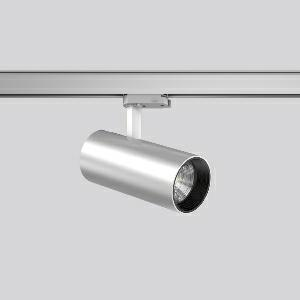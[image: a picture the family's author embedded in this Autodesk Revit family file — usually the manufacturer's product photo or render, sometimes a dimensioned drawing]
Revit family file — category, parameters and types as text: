
# Revit family: deecos_s_mini_742198_004_1_76_52b8
name_source: partatom
category: Lighting Fixtures
units: mm (PartAtom-declared; Revit-internal decimal feet)

## family parameters
Cut with Voids When Loaded = No
Host = Face
Light Source = No
Part Type = Normal
Room Calculation Point = No
Round Connector Dimension = Use Diameter
Shared = No

## types (1)
- DEECOS S mini (1 x LED Modul 940, 2400 lm, 4000)
    Apparent Load = 20 VA
    Approval mark = CE
    CIE Flux Codes = 99 100 100 100 100
    Color Rendering = 92
    Color Temperature = 4000
    Default Elevation = 1800 mm
    Description = Series: DEECOS S mini
LED surface-mounted projector in modern design with no visible cooling ribs. Housing: die-cast aluminium, powder-coated. Rotation range: 356°. Swivel range: 90°. Black plastic ring and recessed LED to prevent glare from the side. Optical assembly with lens made of plastic (polycarbonate) for the best homogeneous light distribution - can be changed without tools. Best colour rendering index Ra>90. With adapter for RZB 3-circuit DALI tracks. Suitable for Track on ceiling, Wall track. High quality converter without flickering and stroboscopic effect. The following accessories can be mounted without use of tools: interchangeable lenses, decorative glasses, honeycomb louvre, clear and frosted diffusers, white interchangeable plastic ring. 
Colour: silver
Diameter: 87 mm
Height: 214 mm
Lamp: LED
Socket: without socket
Colour temperature: 4000K
Colour rendering index (CRI): 92
System power: 20 W
Rated luminous flux: 2400 lm
Luminous efficiency: 120 lm/W
Control gear: Converter, dimmable, DALI
Protection class: I
Type of protection: IP 20
    Height = 214 mm
    Lamp = 1 x LED Modul 940
    Lamp Light Flux = 2400 lm
    Lamp count = 1
    Length = 87 mm
    Lifetime = 50000 h
    Luminous efficacy = 120 lm/W
    Manufacturer = RZB
    ModVariant = No
    Model = 742198.004.1.76
    Mounting Place = Ceiling
    Mounting Type = Rail mounted
    Number of Poles = 1
    OnlyDefault = Yes
    Power Factor = 1
    Product Name = DEECOS S mini
    Product group = Track mounted projectors
    ProductGroupID = 301
    Protection Class = Protection class I
    Protection Degree = IP 20
    RLX_Detail_Level = 1
    RLX_Emergency_Light_Flux = 0 lm
    RLX_Emergency_Type = 0
    RLX_Emergency_Type_DB = No
    RlxData = <blob elided: 37425 chars, md5=33777e1b>
    Socket = socket
    Standby Power = 0 W
    System Light Flux = 2400 lm
    System Power = 20 W
    Type Comments = Product without accessories
    Type Image = 741930.004.jpg
    URL = http://relux.com
    VarID = ---
    Voltage = 230 V
    Voltage Range = 220-240 V
    Weight = 0.00 kg
    Width = 0 mm  [stored 0 ft]

note: [stored X ft] marks values corroborated as IEEE doubles in the binary element streams (Revit-internal decimal feet)

## geometry (parser evidence)
native form markers: Blend x4, Sweep x10
no freeform markers — native parametric forms only
